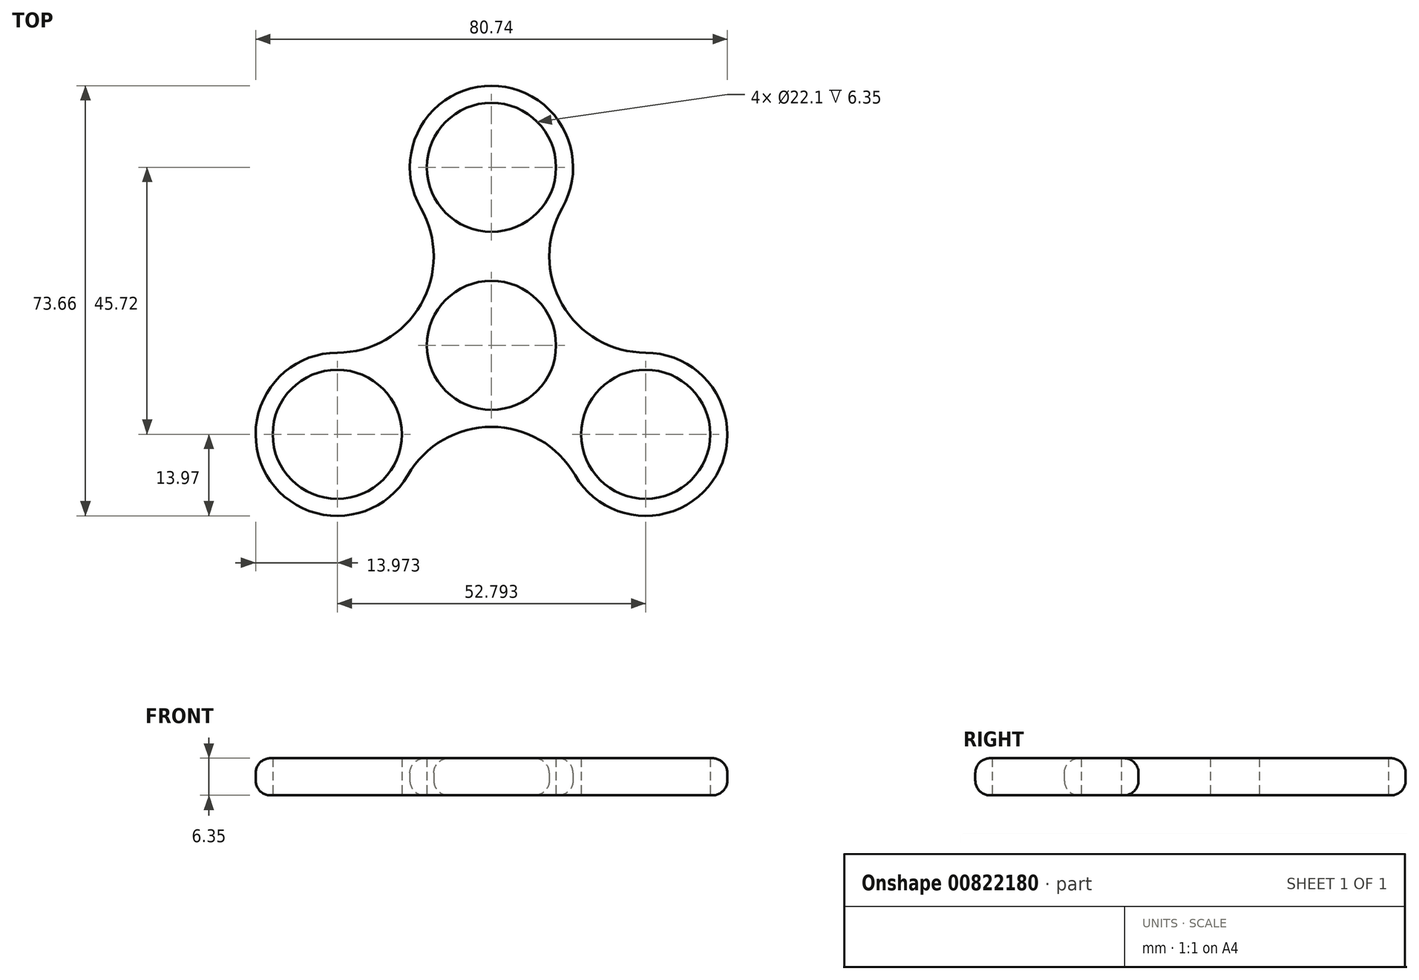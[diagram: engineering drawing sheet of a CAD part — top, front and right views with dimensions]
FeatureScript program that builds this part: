
annotation { "Feature Type Name" : "Feature", "Feature Type Description" : "" }
export const myFeature = defineFeature(function(context is Context, id is Id, definition is map)
    precondition{}
    {
        {
            var Q0;
            Q0=qCreatedBy(makeId("Top.planeOp"),FACE);
            var sketch = newSketch(context, id + "F0", { "sketchPlane" : qUnion([Q0])});
            skCircle(sketch, "E0", {"center": v(0, 0) * mm, "radius": 11.05 * mm});
            skCircle(sketch, "E1", {"center": v(0, 0) * mm, "radius": 13.97 * mm});
            skLineSegment(sketch, "E2", {"start": v(0, 0) * mm, "end": v(0, 30.48) * mm});
            skCircle(sketch, "E3", {"center": v(0, 30.48) * mm, "radius": 11.05 * mm});
            skCircle(sketch, "E4", {"center": v(0, 30.48) * mm, "radius": 13.97 * mm});
            skCircle(sketch, "E5.1.0", {"center": v(-26.4, -15.24) * mm, "radius": 11.05 * mm});
            skCircle(sketch, "E5.1.1", {"center": v(-26.4, -15.24) * mm, "radius": 13.97 * mm});
            skCircle(sketch, "E5.2.0", {"center": v(26.4, -15.24) * mm, "radius": 11.05 * mm});
            skCircle(sketch, "E5.2.1", {"center": v(26.4, -15.24) * mm, "radius": 13.97 * mm});
            skLineSegment(sketch, "E6", {"start": v(0, 0) * mm, "end": v(-26.4, 15.24) * mm});
            skArc(sketch, "E7", {"start": v(-26.4, -1.27) * mm, "mid": v(-12.1, 6.99) * mm, "end": v(-12.1, 23.5) * mm});
            skArc(sketch, "E8.1.0", {"start": v(14.3, -22.23) * mm, "mid": v(0, -13.97) * mm, "end": v(-14.3, -22.22) * mm});
            skArc(sketch, "E8.2.0", {"start": v(12.1, 23.5) * mm, "mid": v(12.1, 6.98) * mm, "end": v(26.4, -1.27) * mm});
            skSolve(sketch);
        }
        {
            var Q0;
            Q0=qSketchRegion(id+"F0",true);
            extrude(context, id + "F1", {"entities" : qUnion([Q0]), "depth" : 6.35 * mm, "offsetDistance" : 25.4 * mm});
        }
        {
            var Q0;
            Q0=makeQuery(id+"F1.opExtrude","CAP_EDGE",EDGE,{"disambiguationData":[OSD([sQuery(id+"F0.wireOp",EDGE,"E8.1.0")])],"isStart":false});
            var Q1;
            Q1=makeQuery(id+"F1.opExtrude","CAP_EDGE",EDGE,{"disambiguationData":[OSD([sQuery(id+"F0.wireOp",EDGE,"E8.1.0")])],"isStart":true});
            fillet(context, id + "F2", {"entities" : qUnion([Q0, Q1]), "radius" : 2.54 * mm, "tangentPropagation" : true, "allowEdgeOverflow" : false});
        }
    });
